# Revit family: IS_Tesi_A6575_BIM_GB
name_source: partatom
category: Plumbing Fixtures
revit_build: Autodesk Revit MEP 2014 (Build: 20130308_1515(x64)
units: mm (PartAtom-declared; Revit-internal decimal feet)

## types (1)
- A6575AA - Tesi Single Lever Tall Basin Mixer - Smooth Body - 5Lpm Eco Flow Regulator
    AccessibilityPerformance = Lever handle
    Accessories = www.idealspec.co.uk
    AreaUnits = millimeters
    Assembly Code = C1030200
    AssetType = Fixed
    BIMObjectName = ISI_IdealStandard_MixerTaps_Tesi_A6575
    BREEAMApproved = No
    Brand = Ideal Standard
    CWFU = 0
    Color = Chrome
    ConnectionType = Plumbing
    Cost = 0 $
    Default Elevation = 0 mm  [stored 0 ft]
    Description = Tesi single lever tall basin mixer
    DurationUnit = year
    ECA = No
    ExpectedLife = 30
    FaucetFunction = MIXED
    FaucetOperation = LEVERHANDLE
    FaucetType = PILLAR
    Features = Single lever, tall basin mixer, smooth body, 5L/m eco flow regulator
    Finish = Chrome
    FlowRate = 5L/min @ 3 bar
    HWFU = 0
    Help = www.idealspec.co.uk/contact-us.html
    IfcExportAs = IfcValveType
    IfcExportType = FAUCET
    InstallationInstructions = www.idealspec.co.uk/resources.html
    LinearUnits = millimeters
    ManufacturerURL = www.idealspec.co.uk
    Material = Brass
    MetalMtl = ISI_IDealStandard_Brassware_Chrome_Render
    Model = A6575AA
    ModelNumber = A6575AA
    ModelReference = Tesi single lever tall basin mixer
    NBSDescription = Water supply fittings for wash basins and troughs
    NBSReference = 45-35-70/371
    Name = MixerTaps_Tesi_A6575_IdealStandard
    NettWeight = 1.74 Kg
    NominalHeight = 301 mm  [stored 0.987533 ft]
    NominalLength = 186 mm
    NominalWidth = 50 mm
    ProductInformation = www.idealspec.co.uk/assets/datasheet/A6575AA
    Shape = Sculptured
    Size = 300 x 185 x 50 mm
    Space = Internal
    SpareParts = www.fastpart-spares.co.uk
    TMV3 = No
    TestPressure = 10 Bar
    URL = www.idealspec.co.uk
    Uniclass2015Description = Water supply fittings for wash basins and troughs
    Uniclass2015Reference = Pr_40_20_87_98
    Uniclass2015Version = Products v1.1
    ValveMechanism = Other
    ValveOperation = Lever
    Version = 1
    VolumeUnits = Litres
    WFU = 0
    WRAS = No
    WarrantyDescription = Manufacturers Warranty
    WarrantyDurationParts = 5
    WarrantyDurationUnit = year
    WaterEfficientProduct = No
    WorkingPressure = 3 Bar

note: [stored X ft] marks values corroborated as IEEE doubles in the binary element streams (Revit-internal decimal feet)

## geometry (parser evidence)
native form markers: Sweep x3
no freeform markers — native parametric forms only
